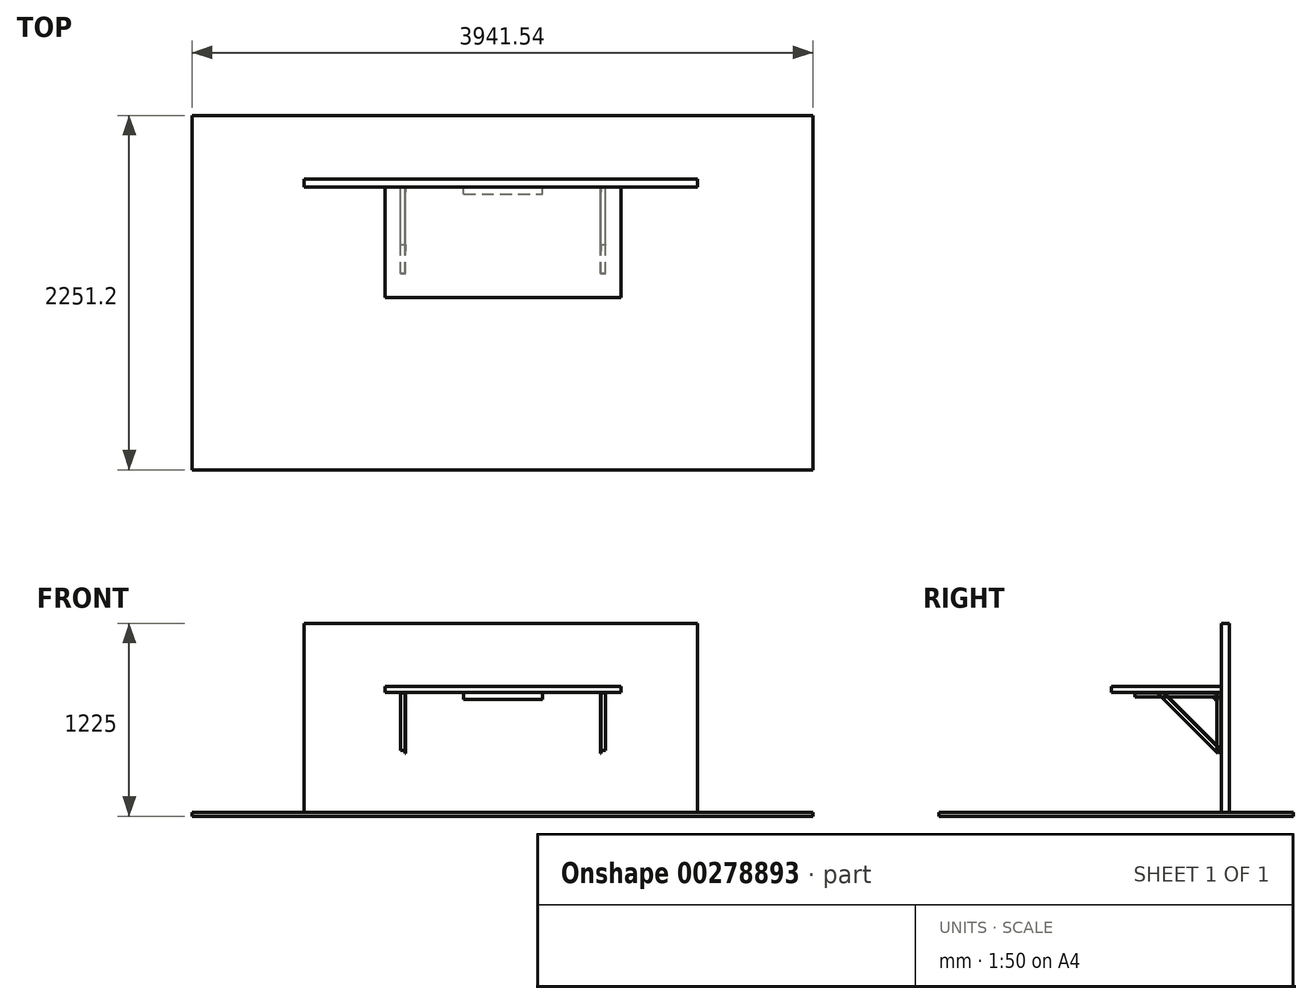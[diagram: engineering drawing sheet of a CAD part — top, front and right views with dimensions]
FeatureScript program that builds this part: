
annotation { "Feature Type Name" : "Feature", "Feature Type Description" : "" }
export const myFeature = defineFeature(function(context is Context, id is Id, definition is map)
    precondition{}
    {
        {
            var Q0;
            Q0=qCreatedBy(makeId("Front.planeOp"),FACE);
            var sketch = newSketch(context, id + "F0", { "sketchPlane" : qUnion([Q0])});
            skLineSegment(sketch, "E0.bottom", {"start": v(0, 0) * mm, "end": v(2500, 0) * mm});
            skLineSegment(sketch, "E0.top", {"start": v(0, 1200) * mm, "end": v(2500, 1200) * mm});
            skLineSegment(sketch, "E0.left", {"start": v(0, 0) * mm, "end": v(0, 1200) * mm});
            skLineSegment(sketch, "E0.right", {"start": v(2500, 0) * mm, "end": v(2500, 1200) * mm});
            skSolve(sketch);
        }
        {
            var Q0;
            Q0 = qSketchRegion(id + "F0", true);
            extrude(context, id + "F1", {"entities" : qUnion([Q0]), "oppositeDirection" : true, "depth" : 50 * mm});
        }
        {
            var Q0;
            Q0=qCreatedBy(makeId("Top.planeOp"),FACE);
            var sketch = newSketch(context, id + "F2", { "sketchPlane" : qUnion([Q0])});
            skLineSegment(sketch, "E1.bottom", {"start": v(-708.85, 455.65) * mm, "end": v(3232.69, 455.65) * mm});
            skLineSegment(sketch, "E1.top", {"start": v(-708.85, -1795.55) * mm, "end": v(3232.69, -1795.55) * mm});
            skLineSegment(sketch, "E1.left", {"start": v(-708.85, 455.65) * mm, "end": v(-708.85, -1795.55) * mm});
            skLineSegment(sketch, "E1.right", {"start": v(3232.69, 455.65) * mm, "end": v(3232.69, -1795.55) * mm});
            skSolve(sketch);
        }
        {
            var Q0;
            Q0 = qSketchRegion(id + "F2", true);
            extrude(context, id + "F3", {"entities" : qUnion([Q0]), "oppositeDirection" : true, "depth" : 25 * mm});
        }
        {
            var Q0;
            Q0=qCreatedBy(makeId("Top.planeOp"),FACE);
            cPlane(context, id + "F4", {"entities" : qUnion([Q0]), "cplaneType" : CPlaneType.OFFSET, "offset" : 800 * mm, "width" : 150 * mm, "height" : 150 * mm});
        }
        {
            var Q0;
            Q0=qCreatedBy(id+"F4.planeOp",FACE);
            var sketch = newSketch(context, id + "F5", { "sketchPlane" : qUnion([Q0])});
            skLineSegment(sketch, "E2.bottom", {"start": v(515.81, 0) * mm, "end": v(2015.81, 0) * mm});
            skLineSegment(sketch, "E2.top", {"start": v(515.81, -700) * mm, "end": v(2015.81, -700) * mm});
            skLineSegment(sketch, "E2.left", {"start": v(515.81, 0) * mm, "end": v(515.81, -700) * mm});
            skLineSegment(sketch, "E2.right", {"start": v(2015.81, 0) * mm, "end": v(2015.81, -700) * mm});
            skSolve(sketch);
        }
        {
            var Q0;
            Q0 = qSketchRegion(id + "F5", true);
            extrude(context, id + "F6", {"entities" : qUnion([Q0]), "oppositeDirection" : true, "depth" : (3 * 11 + 6) * mm});
        }
        {
            var Q0;
            Q0=makeQuery(id+"F1.opExtrude","CAP_FACE",FACE,{"disambiguationData":[OSD([sQuery(id+"F0.wireOp",EDGE,"E0.bottom"),sQuery(id+"F0.wireOp",EDGE,"E0.top"),sQuery(id+"F0.wireOp",EDGE,"E0.left"),sQuery(id+"F0.wireOp",EDGE,"E0.right")])],"isStart":true});
            var sketch = newSketch(context, id + "F7", { "sketchPlane" : qUnion([Q0])});
            skLineSegment(sketch, "E3.bottom", {"start": v(1015.81, 761) * mm, "end": v(1515.81, 761) * mm});
            skLineSegment(sketch, "E3.top", {"start": v(1015.81, 716) * mm, "end": v(1515.81, 716) * mm});
            skLineSegment(sketch, "E3.left", {"start": v(1015.81, 761) * mm, "end": v(1015.81, 716) * mm});
            skLineSegment(sketch, "E3.right", {"start": v(1515.81, 761) * mm, "end": v(1515.81, 716) * mm});
            skLineSegment(sketch, "E4", {"start": v(1265.81, 761) * mm, "end": v(1265.81, 518.93) * mm, "construction": true});
            skSolve(sketch);
        }
        {
            var Q0;
            Q0 = qSketchRegion(id + "F7", true);
            extrude(context, id + "F8", {"entities" : qUnion([Q0]), "depth" : 45 * mm});
        }
        {
            var Q0;
            Q0=makeQuery(id+"F1.opExtrude","CAP_FACE",FACE,{"disambiguationData":[OSD([sQuery(id+"F0.wireOp",EDGE,"E0.bottom"),sQuery(id+"F0.wireOp",EDGE,"E0.top"),sQuery(id+"F0.wireOp",EDGE,"E0.left"),sQuery(id+"F0.wireOp",EDGE,"E0.right")])],"isStart":true});
            var sketch = newSketch(context, id + "F9", { "sketchPlane" : qUnion([Q0])});
            skLineSegment(sketch, "E5", {"start": v(615.81, 761) * mm, "end": v(645.81, 761) * mm});
            skLineSegment(sketch, "E6", {"start": v(645.81, 761) * mm, "end": v(645.81, 731) * mm});
            skLineSegment(sketch, "E7", {"start": v(645.81, 731) * mm, "end": v(642.81, 731) * mm});
            skLineSegment(sketch, "E8", {"start": v(642.81, 731) * mm, "end": v(642.81, 758) * mm});
            skLineSegment(sketch, "E9", {"start": v(642.81, 758) * mm, "end": v(615.81, 758) * mm});
            skLineSegment(sketch, "E10", {"start": v(615.81, 758) * mm, "end": v(615.81, 761) * mm});
            skLineSegment(sketch, "E11", {"start": v(1915.81, 761) * mm, "end": v(1885.81, 761) * mm});
            skLineSegment(sketch, "E12", {"start": v(1885.81, 761) * mm, "end": v(1885.81, 731) * mm});
            skLineSegment(sketch, "E13", {"start": v(1885.81, 731) * mm, "end": v(1888.81, 731) * mm});
            skLineSegment(sketch, "E14", {"start": v(1888.81, 731) * mm, "end": v(1888.81, 758) * mm});
            skLineSegment(sketch, "E15", {"start": v(1888.81, 758) * mm, "end": v(1915.81, 758) * mm});
            skLineSegment(sketch, "E16", {"start": v(1915.81, 758) * mm, "end": v(1915.81, 761) * mm});
            skSolve(sketch);
        }
        {
            var Q0;
            Q0 = qSketchRegion(id + "F9", true);
            extrude(context, id + "F10", {"entities" : qUnion([Q0]), "depth" : 550 * mm});
        }
        {
            var Q0;
            Q0=makeQuery(id+"F6.opExtrude","CAP_FACE",FACE,{"disambiguationData":[OSD([sQuery(id+"F5.wireOp",EDGE,"E2.bottom"),sQuery(id+"F5.wireOp",EDGE,"E2.top"),sQuery(id+"F5.wireOp",EDGE,"E2.left"),sQuery(id+"F5.wireOp",EDGE,"E2.right")])],"isStart":false});
            var sketch = newSketch(context, id + "F11", { "sketchPlane" : qUnion([Q0])});
            skLineSegment(sketch, "E17", {"start": v(615.81, 0) * mm, "end": v(645.81, 0) * mm});
            skLineSegment(sketch, "E18", {"start": v(645.81, 0) * mm, "end": v(645.81, 30) * mm});
            skLineSegment(sketch, "E19", {"start": v(645.81, 30) * mm, "end": v(642.81, 30) * mm});
            skLineSegment(sketch, "E20", {"start": v(642.81, 30) * mm, "end": v(642.81, 3) * mm});
            skLineSegment(sketch, "E21", {"start": v(642.81, 3) * mm, "end": v(615.63, 3) * mm});
            skLineSegment(sketch, "E22", {"start": v(615.63, 3) * mm, "end": v(615.81, 0) * mm});
            skLineSegment(sketch, "E23", {"start": v(1885.81, 30) * mm, "end": v(1885.81, 0) * mm});
            skLineSegment(sketch, "E24", {"start": v(1885.81, 0) * mm, "end": v(1915.81, 0) * mm});
            skLineSegment(sketch, "E25", {"start": v(1915.81, 0) * mm, "end": v(1915.81, 3) * mm});
            skLineSegment(sketch, "E26", {"start": v(1915.81, 3) * mm, "end": v(1888.81, 3) * mm});
            skLineSegment(sketch, "E27", {"start": v(1888.81, 3) * mm, "end": v(1888.81, 30) * mm});
            skLineSegment(sketch, "E28", {"start": v(1888.81, 30) * mm, "end": v(1885.81, 30) * mm});
            skSolve(sketch);
        }
        {
            var Q0;
            Q0 = qSketchRegion(id + "F11", true);
            extrude(context, id + "F12", {"entities" : qUnion([Q0]), "depth" : 368 * mm});
        }
        {
            var Q0;
            Q0=makeQuery(id+"F12.opExtrude","CAP_EDGE",EDGE,{"disambiguationData":[OSD([sQuery(id+"F11.wireOp",EDGE,"E21")])],"isStart":false});
            var Q1;
            Q1=makeQuery(id+"F12.opExtrude","CAP_VERTEX",VERTEX,{"disambiguationData":[OSD([sQuery(id+"F11.wireOp",EDGE,"E19"),sQuery(id+"F11.wireOp",EDGE,"E20")])],"isStart":false});
            cPlane(context, id + "F13", {"entities" : qUnion([Q0, Q1]), "cplaneType" : CPlaneType.LINE_ANGLE, "offset" : 25 * mm, "angle" : 45 * degree, "oppositeDirection" : true, "width" : 150 * mm, "height" : 150 * mm});
        }
        {
            var Q0;
            Q0=qCreatedBy(id+"F13.planeOp",FACE);
            var sketch = newSketch(context, id + "F14", { "sketchPlane" : qUnion([Q0])});
            skLineSegment(sketch, "E29", {"start": v(645.63, 248.78) * mm, "end": v(645.63, 278.78) * mm});
            skLineSegment(sketch, "E30", {"start": v(645.63, 278.78) * mm, "end": v(615.63, 278.78) * mm});
            skLineSegment(sketch, "E31", {"start": v(615.63, 278.78) * mm, "end": v(615.63, 275.78) * mm});
            skLineSegment(sketch, "E32", {"start": v(615.63, 275.78) * mm, "end": v(642.63, 275.78) * mm});
            skLineSegment(sketch, "E33", {"start": v(642.63, 275.78) * mm, "end": v(642.63, 248.78) * mm});
            skLineSegment(sketch, "E34", {"start": v(642.63, 248.78) * mm, "end": v(645.63, 248.78) * mm});
            skLineSegment(sketch, "E35", {"start": v(1915.81, 278.77) * mm, "end": v(1885.81, 278.77) * mm});
            skLineSegment(sketch, "E36", {"start": v(1885.81, 278.77) * mm, "end": v(1885.81, 248.77) * mm});
            skLineSegment(sketch, "E37", {"start": v(1885.81, 248.77) * mm, "end": v(1888.81, 248.77) * mm});
            skLineSegment(sketch, "E38", {"start": v(1888.81, 248.77) * mm, "end": v(1888.81, 275.77) * mm});
            skLineSegment(sketch, "E39", {"start": v(1888.81, 275.77) * mm, "end": v(1915.81, 275.77) * mm});
            skLineSegment(sketch, "E40", {"start": v(1915.81, 275.77) * mm, "end": v(1915.81, 278.77) * mm});
            skSolve(sketch);
        }
        {
            var Q0;
            Q0 = qSketchRegion(id + "F14", true);
            var Q1;
            Q1=makeQuery(id+"F10.opExtrude","SWEPT_FACE",FACE,{"disambiguationData":[OSD([sQuery(id+"F9.wireOp",EDGE,"E9")])]});
            extrude(context, id + "F15", {"entities" : qUnion([Q0]), "endBound" : BoundingType.UP_TO_SURFACE, "endBoundEntityFace" : qUnion([Q1]), "depth" : 473 * mm});
        }
    });
